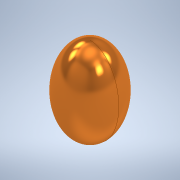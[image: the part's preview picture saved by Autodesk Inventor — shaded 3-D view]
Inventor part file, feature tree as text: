
AUTODESK INVENTOR PART (.ipt)
format: ipt  version: 2020 (Build 240168000, 168)  size: 227,328 bytes
history: native  units: mm
features: revolve x1, sketch x1
ambient origin geometry x8: Origin, YZ Plane, XZ Plane, XY Plane, X Axis, Y Axis, Z Axis, Center Point
bodies: Volumenkörper1 (feature_tree)
feature tree (2):
  revolve  "Umdrehung1"
  sketch  "Skizze1"  dims[d0=30.0mm d1=45.0mm d2=180.0deg]
